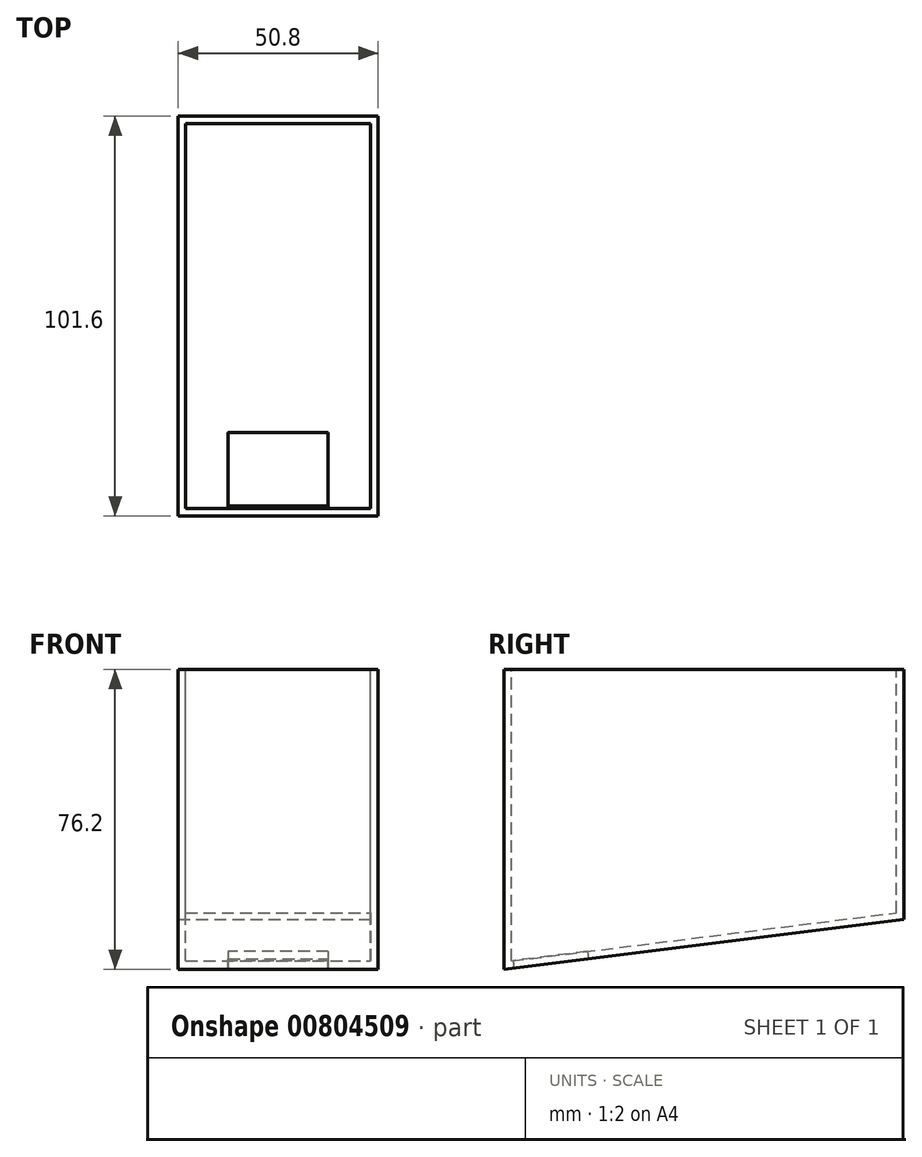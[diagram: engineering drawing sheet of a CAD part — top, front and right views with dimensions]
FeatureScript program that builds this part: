
annotation { "Feature Type Name" : "Feature", "Feature Type Description" : "" }
export const myFeature = defineFeature(function(context is Context, id is Id, definition is map)
    precondition{}
    {
        {
            var Q0;
            Q0=qCreatedBy(makeId("Front.planeOp"),FACE);
            var sketch = newSketch(context, id + "F0", { "sketchPlane" : qUnion([Q0])});
            skLineSegment(sketch, "E0.bottom", {"start": v(0, 0) * mm, "end": v(50.8, 0) * mm});
            skLineSegment(sketch, "E0.top", {"start": v(0, 76.2) * mm, "end": v(50.8, 76.2) * mm});
            skLineSegment(sketch, "E0.left", {"start": v(0, 0) * mm, "end": v(0, 76.2) * mm});
            skLineSegment(sketch, "E0.right", {"start": v(50.8, 0) * mm, "end": v(50.8, 76.2) * mm});
            skSolve(sketch);
        }
        {
            var Q0;
            Q0=makeQuery(id+"F0.imprint","IMPRINT",FACE,{"disambiguationData":[TD([[makeQuery(id+"F0.imprint","IMPRINT",EDGE,{"derivedFrom":sQuery(id+"F0.wireOp",EDGE,"E0.bottom")}),1.0]])]});
            extrude(context, id + "F1", {"entities" : qUnion([Q0]), "depth" : 101.6 * mm, "offsetDistance" : 25.4 * mm});
        }
        {
            var Q0;
            Q0=makeQuery(id+"F1.opExtrude","SWEPT_FACE",FACE,{"disambiguationData":[OSD([sQuery(id+"F0.wireOp",EDGE,"E0.right")])]});
            var sketch = newSketch(context, id + "F2", { "sketchPlane" : qUnion([Q0])});
            skLineSegment(sketch, "E1", {"start": v(0, 0) * mm, "end": v(0, 12.7) * mm});
            skLineSegment(sketch, "E2", {"start": v(0, 12.7) * mm, "end": v(-101.6, 0) * mm});
            skLineSegment(sketch, "E3", {"start": v(-101.6, 0) * mm, "end": v(0, 0) * mm});
            skSolve(sketch);
        }
        {
            var Q0;
            Q0=makeQuery(id+"F2.imprint","IMPRINT",FACE,{"disambiguationData":[TD([[makeQuery(id+"F2.imprint","IMPRINT",EDGE,{"derivedFrom":sQuery(id+"F2.wireOp",EDGE,"E1")}),1.0]])]});
            extrude(context, id + "F3", {"entities" : qUnion([Q0]), "operationType" : NewBodyOperationType.REMOVE, "endBound" : BoundingType.THROUGH_ALL, "oppositeDirection" : true, "depth" : 25.4 * mm, "offsetDistance" : 25.4 * mm});
        }
        {
            var Q0;
            Q0=makeQuery(id+"F1.opExtrude","SWEPT_FACE",FACE,{"disambiguationData":[OSD([sQuery(id+"F0.wireOp",EDGE,"E0.top")])]});
            shell(context, id + "F4", {"entities" : qUnion([Q0]), "thickness" : 1.9 * mm});
        }
        {
            var Q0;
            Q0=makeQuery(id+"F3.boolean.opBoolean","COPY",FACE,{"derivedFrom":makeQuery(id+"F3.opExtrude","SWEPT_FACE",FACE,{"disambiguationData":[OSD([sQuery(id+"F2.wireOp",EDGE,"E2")])]})});
            var sketch = newSketch(context, id + "F5", { "sketchPlane" : qUnion([Q0])});
            skLineSegment(sketch, "E4", {"start": v(0, 100.82) * mm, "end": v(12.7, 100.82) * mm, "construction": true});
            skLineSegment(sketch, "E5", {"start": v(12.7, 100.82) * mm, "end": v(38.1, 100.82) * mm, "construction": true});
            skLineSegment(sketch, "E6", {"start": v(38.1, 100.82) * mm, "end": v(38.1, 98.28) * mm, "construction": true});
            skLineSegment(sketch, "E7", {"start": v(38.1, 98.28) * mm, "end": v(12.7, 98.28) * mm, "construction": true});
            skLineSegment(sketch, "E8", {"start": v(12.7, 98.28) * mm, "end": v(12.7, 100.82) * mm, "construction": true});
            skLineSegment(sketch, "E9", {"start": v(12.7, 98.28) * mm, "end": v(12.7, 79.23) * mm, "construction": true});
            skLineSegment(sketch, "E10", {"start": v(12.7, 79.23) * mm, "end": v(38.1, 79.23) * mm, "construction": true});
            skLineSegment(sketch, "E11", {"start": v(38.1, 79.23) * mm, "end": v(38.1, 98.28) * mm, "construction": true});
            skLineSegment(sketch, "E12.bottom", {"start": v(12.7, 98.28) * mm, "end": v(38.1, 98.28) * mm});
            skLineSegment(sketch, "E12.top", {"start": v(12.7, 79.23) * mm, "end": v(38.1, 79.23) * mm});
            skLineSegment(sketch, "E12.left", {"start": v(12.7, 98.28) * mm, "end": v(12.7, 79.23) * mm});
            skLineSegment(sketch, "E12.right", {"start": v(38.1, 98.28) * mm, "end": v(38.1, 79.23) * mm});
            skSolve(sketch);
        }
        {
            var Q0;
            Q0 = qSketchRegion(id + "F5", true);
            extrude(context, id + "F6", {"entities" : qUnion([Q0]), "operationType" : NewBodyOperationType.REMOVE, "oppositeDirection" : true, "depth" : 3.05 * mm, "offsetDistance" : 25.4 * mm});
        }
    });
